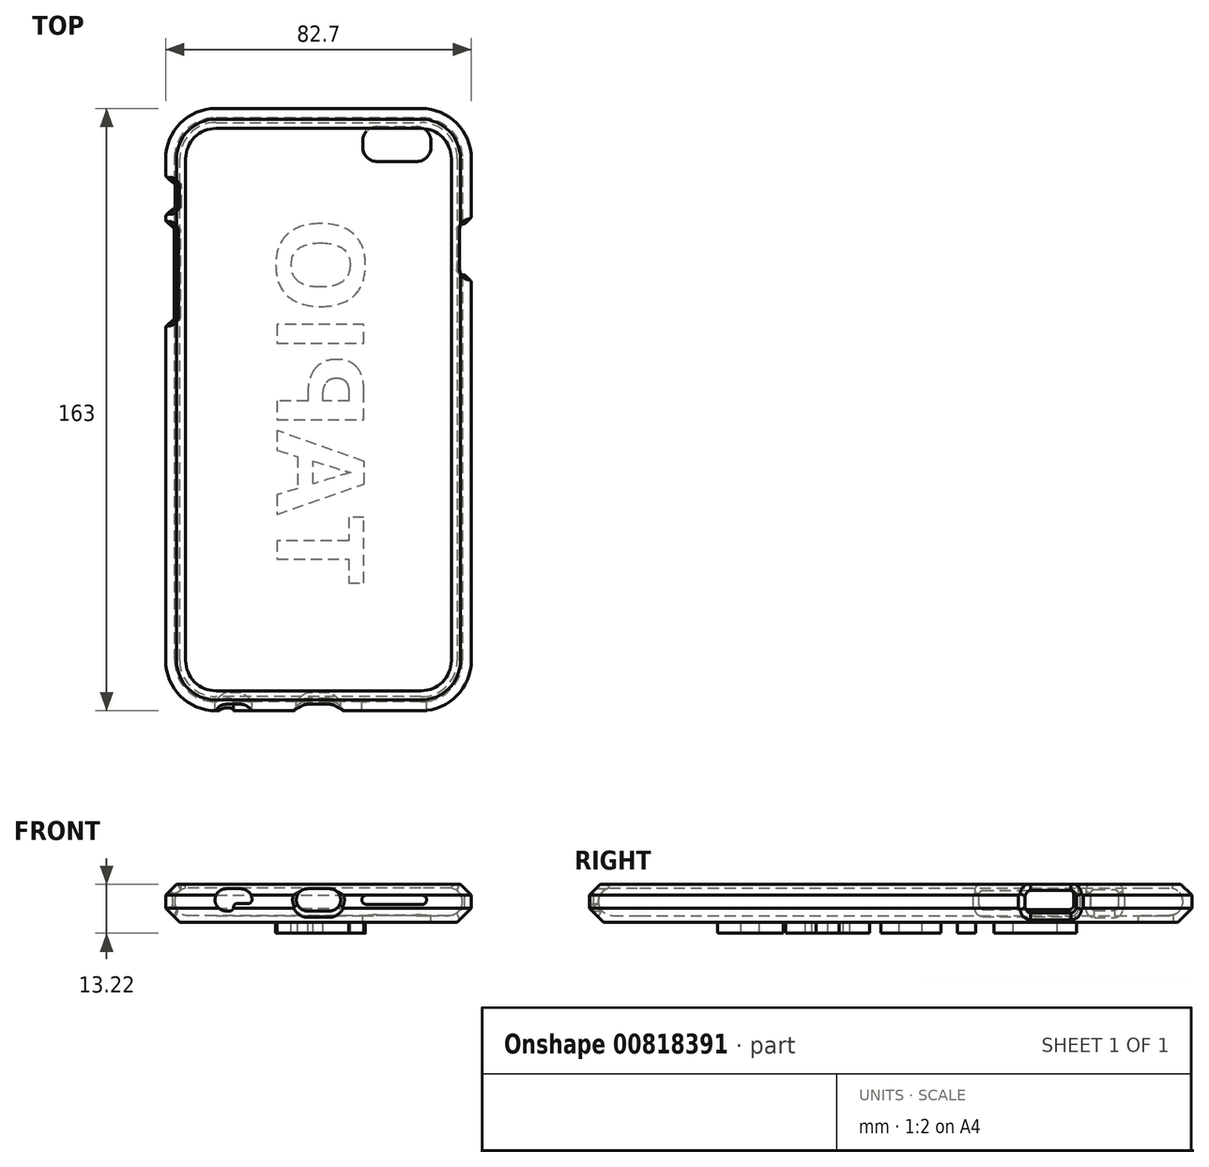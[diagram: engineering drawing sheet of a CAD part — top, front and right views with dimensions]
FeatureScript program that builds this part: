
annotation { "Feature Type Name" : "Feature", "Feature Type Description" : "" }
export const myFeature = defineFeature(function(context is Context, id is Id, definition is map)
    precondition{}
    {
        {
            assignVariable(context, id + "F0", {"name" : "HoleChamferLength", "anyValue" : 1.25});
        }
        {
            assignVariable(context, id + "F1", {"name" : "HoleChamferTopBottom", "anyValue" : 1.75});
        }
        {
            var Q0;
            Q0=qCreatedBy(makeId("Top.planeOp"),FACE);
            var sketch = newSketch(context, id + "F2", { "sketchPlane" : qUnion([Q0])});
            skLineSegment(sketch, "E0.bottom", {"start": v(27.75, 79.1) * mm, "end": v(0, 79.1) * mm});
            skLineSegment(sketch, "E0.top", {"start": v(27.75, -79.1) * mm, "end": v(-27.75, -79.1) * mm});
            skLineSegment(sketch, "E0.left", {"start": v(38.95, 67.9) * mm, "end": v(38.95, -67.9) * mm});
            skLineSegment(sketch, "E0.right", {"start": v(-38.95, 67.9) * mm, "end": v(-38.95, -67.9) * mm});
            skPoint(sketch, "E0.middle", {"position": v(0, 0) * mm});
            skPoint(sketch, "E1.visualSharp", {"position": v(-38.95, 79.1) * mm});
            skArc(sketch, "E1.filletArc", {"start": v(-27.75, 79.1) * mm, "mid": v(-35.67, 75.82) * mm, "end": v(-38.95, 67.9) * mm});
            skPoint(sketch, "E2.visualSharp", {"position": v(38.95, 79.1) * mm});
            skArc(sketch, "E2.filletArc", {"start": v(38.95, 67.9) * mm, "mid": v(35.67, 75.82) * mm, "end": v(27.75, 79.1) * mm});
            skPoint(sketch, "E3.visualSharp", {"position": v(38.95, -79.1) * mm});
            skArc(sketch, "E3.filletArc", {"start": v(27.75, -79.1) * mm, "mid": v(35.67, -75.82) * mm, "end": v(38.95, -67.9) * mm});
            skPoint(sketch, "E4.visualSharp", {"position": v(-38.95, -79.1) * mm});
            skArc(sketch, "E4.filletArc", {"start": v(-38.95, -67.9) * mm, "mid": v(-35.67, -75.82) * mm, "end": v(-27.75, -79.1) * mm});
            skLineSegment(sketch, "E5", {"start": v(0, 79.1) * mm, "end": v(-27.75, 79.1) * mm});
            skSolve(sketch);
        }
        {
            var Q0;
            Q0=qCreatedBy(makeId("Right.planeOp"),FACE);
            var sketch = newSketch(context, id + "F3", { "sketchPlane" : qUnion([Q0])});
            skPoint(sketch, "E6.0", {"position": v(79.1, 0) * mm});
            skArc(sketch, "E7", {"start": v(75.35, -3.75) * mm, "mid": v(79.1, 0) * mm, "end": v(75.35, 3.75) * mm});
            skLineSegment(sketch, "E8", {"start": v(75.35, -3.75) * mm, "end": v(75.35, 3.75) * mm, "construction": true});
            skLineSegment(sketch, "E9", {"start": v(81.5, -1.75) * mm, "end": v(81.5, 1.75) * mm});
            skLineSegment(sketch, "E10", {"start": v(81.5, 1.75) * mm, "end": v(79.75, 3.5) * mm});
            skLineSegment(sketch, "E11.trimOffspring", {"start": v(79.75, -3.5) * mm, "end": v(81.5, -1.75) * mm});
            skLineSegment(sketch, "E12", {"start": v(75.35, -5.55) * mm, "end": v(75.35, -3.75) * mm});
            skLineSegment(sketch, "E13", {"start": v(75.35, -5.55) * mm, "end": v(84.8, -5.55) * mm, "construction": true});
            skPoint(sketch, "E14", {"position": v(81.5, 0) * mm});
            skPoint(sketch, "E15.visualSharp", {"position": v(66.64, 4.7) * mm});
            skArc(sketch, "E15.filletArc", {"start": v(77.32, 4.67) * mm, "mid": v(76.53, 4.4) * mm, "end": v(76.1, 3.67) * mm});
            skLineSegment(sketch, "E16", {"start": v(79.75, -3.5) * mm, "end": v(77.7, -5.55) * mm});
            skLineSegment(sketch, "E17", {"start": v(77.7, -5.55) * mm, "end": v(75.35, -5.55) * mm});
            skLineSegment(sketch, "E18", {"start": v(79.75, 3.5) * mm, "end": v(78.58, 4.67) * mm});
            skLineSegment(sketch, "E19", {"start": v(78.58, 4.67) * mm, "end": v(77.32, 4.67) * mm});
            skLineSegment(sketch, "E20", {"start": v(76.1, 3.67) * mm, "end": v(66.64, 5.6) * mm, "construction": true});
            skSolve(sketch);
        }
        {
            var Q0;
            Q0=sQuery(id+"F2.wireOp",EDGE,"E5");
            var Q1;
            Q1=sQuery(id+"F2.wireOp",VERTEX,"E5.end");
            cPlane(context, id + "F4", {"entities" : qUnion([Q0, Q1]), "cplaneType" : CPlaneType.LINE_POINT, "offset" : 25 * mm, "width" : 150 * mm, "height" : 150 * mm});
        }
        {
            var Q0;
            Q0=sQuery(id+"F2.wireOp",EDGE,"E0.bottom");
            var Q1;
            Q1=sQuery(id+"F2.wireOp",VERTEX,"E2.filletArc.end");
            cPlane(context, id + "F5", {"entities" : qUnion([Q0, Q1]), "cplaneType" : CPlaneType.LINE_POINT, "offset" : 25 * mm, "width" : 150 * mm, "height" : 150 * mm});
        }
        {
            var Q0;
            Q0=sQuery(id+"F2.wireOp",EDGE,"E0.right");
            var Q1;
            Q1=sQuery(id+"F2.wireOp",VERTEX,"E0.right.end");
            cPlane(context, id + "F6", {"entities" : qUnion([Q0, Q1]), "cplaneType" : CPlaneType.LINE_POINT, "offset" : 25 * mm, "width" : 150 * mm, "height" : 150 * mm});
        }
        {
            var Q0;
            Q0=qCreatedBy(id+"F4.planeOp",FACE);
            var sketch = newSketch(context, id + "F7", { "sketchPlane" : qUnion([Q0])});
            skLineSegment(sketch, "E21.bottom", {"start": v(-24.95, -1.88) * mm, "end": v(-48.6, -1.88) * mm});
            skLineSegment(sketch, "E21.top", {"start": v(-24.95, 2.87) * mm, "end": v(-48.6, 2.87) * mm});
            skLineSegment(sketch, "E21.left", {"start": v(-23.95, -0.88) * mm, "end": v(-23.95, 1.87) * mm});
            skLineSegment(sketch, "E21.right", {"start": v(-49.6, -0.88) * mm, "end": v(-49.6, 1.87) * mm});
            skPoint(sketch, "E21.middle", {"position": v(-36.77, 0.5) * mm});
            skPoint(sketch, "E22.visualSharp", {"position": v(-49.6, 2.87) * mm});
            skArc(sketch, "E22.filletArc", {"start": v(-48.6, 2.87) * mm, "mid": v(-49.3, 2.58) * mm, "end": v(-49.6, 1.87) * mm});
            skPoint(sketch, "E23.visualSharp", {"position": v(-49.6, -1.88) * mm});
            skArc(sketch, "E23.filletArc", {"start": v(-49.6, -0.88) * mm, "mid": v(-49.3, -1.58) * mm, "end": v(-48.6, -1.88) * mm});
            skPoint(sketch, "E24.visualSharp", {"position": v(-23.95, 2.87) * mm});
            skArc(sketch, "E24.filletArc", {"start": v(-23.95, 1.87) * mm, "mid": v(-24.24, 2.58) * mm, "end": v(-24.95, 2.87) * mm});
            skPoint(sketch, "E25.visualSharp", {"position": v(-23.95, -1.88) * mm});
            skArc(sketch, "E25.filletArc", {"start": v(-24.95, -1.88) * mm, "mid": v(-24.24, -1.58) * mm, "end": v(-23.95, -0.88) * mm});
            skLineSegment(sketch, "E26.bottom", {"start": v(-60.6, 3.12) * mm, "end": v(-55.1, 3.12) * mm});
            skLineSegment(sketch, "E26.top", {"start": v(-60.6, -2.13) * mm, "end": v(-55.1, -2.13) * mm});
            skLineSegment(sketch, "E26.left", {"start": v(-61.6, 2.12) * mm, "end": v(-61.6, -1.13) * mm});
            skLineSegment(sketch, "E26.right", {"start": v(-54.1, 2.12) * mm, "end": v(-54.1, -1.13) * mm});
            skPoint(sketch, "E26.middle", {"position": v(-57.85, 0.5) * mm});
            skPoint(sketch, "E27.visualSharp", {"position": v(-61.6, 3.12) * mm});
            skArc(sketch, "E27.filletArc", {"start": v(-60.6, 3.13) * mm, "mid": v(-61.3, 2.83) * mm, "end": v(-61.6, 2.12) * mm});
            skPoint(sketch, "E28.visualSharp", {"position": v(-61.6, -2.13) * mm});
            skArc(sketch, "E28.filletArc", {"start": v(-61.6, -1.13) * mm, "mid": v(-61.3, -1.83) * mm, "end": v(-60.6, -2.13) * mm});
            skPoint(sketch, "E29.visualSharp", {"position": v(-54.1, -2.13) * mm});
            skArc(sketch, "E29.filletArc", {"start": v(-55.1, -2.13) * mm, "mid": v(-54.4, -1.83) * mm, "end": v(-54.1, -1.13) * mm});
            skPoint(sketch, "E30.visualSharp", {"position": v(-54.1, 3.12) * mm});
            skArc(sketch, "E30.filletArc", {"start": v(-54.1, 2.12) * mm, "mid": v(-54.4, 2.83) * mm, "end": v(-55.1, 3.13) * mm});
            skSolve(sketch);
        }
        {
            var Q0;
            Q0=qCreatedBy(id+"F5.planeOp",FACE);
            var sketch = newSketch(context, id + "F8", { "sketchPlane" : qUnion([Q0])});
            skLineSegment(sketch, "E31.bottom", {"start": v(-48.85, 2.75) * mm, "end": v(-37.85, 2.75) * mm});
            skLineSegment(sketch, "E31.top", {"start": v(-48.85, -2.75) * mm, "end": v(-37.85, -2.75) * mm});
            skLineSegment(sketch, "E31.left", {"start": v(-50.35, 1.25) * mm, "end": v(-50.35, -1.25) * mm});
            skLineSegment(sketch, "E31.right", {"start": v(-36.35, 1.25) * mm, "end": v(-36.35, -1.25) * mm});
            skPoint(sketch, "E31.middle", {"position": v(-43.35, 0) * mm});
            skPoint(sketch, "E32.visualSharp", {"position": v(-50.35, 2.75) * mm});
            skArc(sketch, "E32.filletArc", {"start": v(-48.85, 2.75) * mm, "mid": v(-49.91, 2.31) * mm, "end": v(-50.35, 1.25) * mm});
            skPoint(sketch, "E33.visualSharp", {"position": v(-50.35, -2.75) * mm});
            skArc(sketch, "E33.filletArc", {"start": v(-50.35, -1.25) * mm, "mid": v(-49.91, -2.31) * mm, "end": v(-48.85, -2.75) * mm});
            skPoint(sketch, "E34.visualSharp", {"position": v(-36.35, -2.75) * mm});
            skArc(sketch, "E34.filletArc", {"start": v(-37.85, -2.75) * mm, "mid": v(-36.79, -2.31) * mm, "end": v(-36.35, -1.25) * mm});
            skPoint(sketch, "E35.visualSharp", {"position": v(-36.35, 2.75) * mm});
            skArc(sketch, "E35.filletArc", {"start": v(-36.35, 1.25) * mm, "mid": v(-36.79, 2.31) * mm, "end": v(-37.85, 2.75) * mm});
            skSolve(sketch);
        }
        {
            var Q0;
            Q0=qCreatedBy(id+"F6.planeOp",FACE);
            var sketch = newSketch(context, id + "F9", { "sketchPlane" : qUnion([Q0])});
            skLineSegment(sketch, "E36.bottom", {"start": v(3, 3.5) * mm, "end": v(-3, 3.5) * mm});
            skLineSegment(sketch, "E36.top", {"start": v(3, -2.5) * mm, "end": v(-3, -2.5) * mm});
            skLineSegment(sketch, "E36.left", {"start": v(6, 0.5) * mm, "end": v(6, 0.5) * mm});
            skLineSegment(sketch, "E36.right", {"start": v(-6, 0.5) * mm, "end": v(-6, 0.5) * mm});
            skPoint(sketch, "E36.middle", {"position": v(0, 0.5) * mm});
            skArc(sketch, "E37", {"start": v(-25, 3.5) * mm, "mid": v(-28, 0.5) * mm, "end": v(-25, -2.5) * mm});
            skPoint(sketch, "E38.visualSharp", {"position": v(-6, 3.5) * mm});
            skArc(sketch, "E38.filletArc", {"start": v(-3, 3.5) * mm, "mid": v(-5.12, 2.62) * mm, "end": v(-6, 0.5) * mm});
            skPoint(sketch, "E39.visualSharp", {"position": v(-6, -2.5) * mm});
            skArc(sketch, "E39.filletArc", {"start": v(-6, 0.5) * mm, "mid": v(-5.12, -1.62) * mm, "end": v(-3, -2.5) * mm});
            skPoint(sketch, "E40.visualSharp", {"position": v(6, -2.5) * mm});
            skArc(sketch, "E40.filletArc", {"start": v(3, -2.5) * mm, "mid": v(5.12, -1.62) * mm, "end": v(6, 0.5) * mm});
            skPoint(sketch, "E41.visualSharp", {"position": v(6, 3.5) * mm});
            skArc(sketch, "E41.filletArc", {"start": v(6, 0.5) * mm, "mid": v(5.12, 2.62) * mm, "end": v(3, 3.5) * mm});
            skArc(sketch, "E42", {"start": v(-21, -2.5) * mm, "mid": v(-19.27, -1.95) * mm, "end": v(-18.17, -0.5) * mm, "construction": true});
            skLineSegment(sketch, "E43", {"start": v(-21, 3.5) * mm, "end": v(-25, 3.5) * mm});
            skLineSegment(sketch, "E44", {"start": v(-21, -2.5) * mm, "end": v(-23, -2.5) * mm, "construction": true});
            skLineSegment(sketch, "E45", {"start": v(13, 0.5) * mm, "end": v(28, 0.5) * mm, "construction": true});
            skArc(sketch, "E46.0.startCap", {"start": v(13, -0.75) * mm, "mid": v(11.75, 0.5) * mm, "end": v(13, 1.75) * mm});
            skArc(sketch, "E46.0.endCap", {"start": v(28, 1.75) * mm, "mid": v(29.25, 0.5) * mm, "end": v(28, -0.75) * mm});
            skLineSegment(sketch, "E46.0.left", {"start": v(13, 1.75) * mm, "end": v(28, 1.75) * mm});
            skLineSegment(sketch, "E46.0.right", {"start": v(13, -0.75) * mm, "end": v(28, -0.75) * mm});
            skLineSegment(sketch, "E47", {"start": v(-23, -1.5) * mm, "end": v(-23, -1.5) * mm});
            skLineSegment(sketch, "E48", {"start": v(-22, -0.5) * mm, "end": v(-19, -0.5) * mm});
            skLineSegment(sketch, "E49", {"start": v(-24, -2.5) * mm, "end": v(-25, -2.5) * mm});
            skArc(sketch, "E50", {"start": v(-18, 0.5) * mm, "mid": v(-18.88, 2.62) * mm, "end": v(-21, 3.5) * mm});
            skPoint(sketch, "E51.visualSharp", {"position": v(-23, -0.5) * mm});
            skArc(sketch, "E51.filletArc", {"start": v(-22, -0.5) * mm, "mid": v(-22.7, -0.8) * mm, "end": v(-23, -1.5) * mm});
            skPoint(sketch, "E52.visualSharp", {"position": v(-23, -2.5) * mm});
            skArc(sketch, "E52.filletArc", {"start": v(-24, -2.5) * mm, "mid": v(-23.3, -2.2) * mm, "end": v(-23, -1.5) * mm});
            skPoint(sketch, "E53.visualSharp", {"position": v(-18.17, -0.5) * mm});
            skArc(sketch, "E53.filletArc", {"start": v(-19, -0.5) * mm, "mid": v(-18.3, -0.2) * mm, "end": v(-18, 0.5) * mm});
            skCircle(sketch, "E54", {"center": v(-25, 0.5) * mm, "radius": 2.5 * mm, "construction": true});
            skSolve(sketch);
        }
        {
            var Q0;
            Q0=qCreatedBy(makeId("Top.planeOp"),FACE);
            var sketch = newSketch(context, id + "F10", { "sketchPlane" : qUnion([Q0])});
            skLineSegment(sketch, "E55.bottom", {"start": v(26.45, 67.1) * mm, "end": v(15.95, 67.1) * mm});
            skLineSegment(sketch, "E55.top", {"start": v(26.45, 76.6) * mm, "end": v(15.95, 76.6) * mm});
            skLineSegment(sketch, "E55.left", {"start": v(30.45, 71.1) * mm, "end": v(30.45, 72.6) * mm});
            skLineSegment(sketch, "E55.right", {"start": v(11.95, 71.1) * mm, "end": v(11.95, 72.6) * mm});
            skPoint(sketch, "E55.middle", {"position": v(21.2, 71.85) * mm});
            skPoint(sketch, "E56.visualSharp", {"position": v(11.95, 76.6) * mm});
            skArc(sketch, "E56.filletArc", {"start": v(15.95, 76.6) * mm, "mid": v(13.12, 75.43) * mm, "end": v(11.95, 72.6) * mm});
            skPoint(sketch, "E57.visualSharp", {"position": v(11.95, 67.1) * mm});
            skArc(sketch, "E57.filletArc", {"start": v(11.95, 71.1) * mm, "mid": v(13.12, 68.27) * mm, "end": v(15.95, 67.1) * mm});
            skPoint(sketch, "E58.visualSharp", {"position": v(30.45, 67.1) * mm});
            skArc(sketch, "E58.filletArc", {"start": v(26.45, 67.1) * mm, "mid": v(29.28, 68.27) * mm, "end": v(30.45, 71.1) * mm});
            skPoint(sketch, "E59.visualSharp", {"position": v(30.45, 76.6) * mm});
            skArc(sketch, "E59.filletArc", {"start": v(30.45, 72.6) * mm, "mid": v(29.28, 75.43) * mm, "end": v(26.45, 76.6) * mm});
            skSolve(sketch);
        }
        {
            var Q0;
            Q0=qSketchRegion(id+"F3",true);
            var Q1;
            Q1=sQuery(id+"F2.wireOp",EDGE,"E5");
            var Q2;
            Q2=sQuery(id+"F2.wireOp",EDGE,"E1.filletArc");
            var Q3;
            Q3=sQuery(id+"F2.wireOp",EDGE,"E0.right");
            var Q4;
            Q4=sQuery(id+"F2.wireOp",EDGE,"E4.filletArc");
            var Q5;
            Q5=sQuery(id+"F2.wireOp",EDGE,"E0.top");
            var Q6;
            Q6=sQuery(id+"F2.wireOp",EDGE,"E3.filletArc");
            var Q7;
            Q7=sQuery(id+"F2.wireOp",EDGE,"E0.left");
            var Q8;
            Q8=sQuery(id+"F2.wireOp",EDGE,"E2.filletArc");
            var Q9;
            Q9=sQuery(id+"F2.wireOp",EDGE,"E0.bottom");
            sweep(context, id + "F11", {"profiles" : qUnion([Q0]), "path" : qUnion([Q1, Q2, Q3, Q4, Q5, Q6, Q7, Q8, Q9])});
        }
        {
            var Q0;
            Q0=qCreatedBy(makeId("Front.planeOp"),FACE);
            var sketch = newSketch(context, id + "F12", { "sketchPlane" : qUnion([Q0])});
            skLineSegment(sketch, "E60.0.0", {"start": v(35.2, -5.55) * mm, "end": v(27.75, -5.55) * mm});
            skLineSegment(sketch, "E60.0.1", {"start": v(27.75, -3.75) * mm, "end": v(27.75, -5.55) * mm});
            skLineSegment(sketch, "E60.0.2", {"start": v(27.75, -3.75) * mm, "end": v(35.2, -3.75) * mm});
            skLineSegment(sketch, "E60.0.3", {"start": v(35.2, -3.75) * mm, "end": v(35.2, -5.55) * mm});
            skLineSegment(sketch, "E60.1.0", {"start": v(27.75, -5.55) * mm, "end": v(-27.75, -5.55) * mm});
            skLineSegment(sketch, "E60.1.1", {"start": v(-27.75, -3.75) * mm, "end": v(-27.75, -5.55) * mm});
            skLineSegment(sketch, "E60.1.2", {"start": v(-27.75, -3.75) * mm, "end": v(27.75, -3.75) * mm});
            skLineSegment(sketch, "E60.1.3", {"start": v(27.75, -3.75) * mm, "end": v(27.75, -5.55) * mm});
            skLineSegment(sketch, "E60.2.0", {"start": v(-27.75, -5.55) * mm, "end": v(-35.2, -5.55) * mm});
            skLineSegment(sketch, "E60.2.1", {"start": v(-35.2, -3.75) * mm, "end": v(-35.2, -5.55) * mm});
            skLineSegment(sketch, "E60.2.2", {"start": v(-35.2, -3.75) * mm, "end": v(-27.75, -3.75) * mm});
            skLineSegment(sketch, "E60.2.3", {"start": v(-27.75, -3.75) * mm, "end": v(-27.75, -5.55) * mm});
            skSolve(sketch);
        }
        {
            var Q0;
            Q0=qSketchRegion(id+"F12",true);
            extrude(context, id + "F13", {"entities" : qUnion([Q0]), "operationType" : NewBodyOperationType.ADD, "endBound" : BoundingType.UP_TO_NEXT, "depth" : 25 * mm, "hasSecondDirection" : true, "secondDirectionBound" : SecondDirectionBoundingType.UP_TO_NEXT, "secondDirectionOppositeDirection" : true, "secondDirectionDepth" : 25 * mm});
        }
        {
            var Q0;
            Q0=qSketchRegion(id+"F7",true);
            extrude(context, id + "F14", {"entities" : qUnion([Q0]), "operationType" : NewBodyOperationType.REMOVE, "endBound" : BoundingType.THROUGH_ALL, "depth" : 25 * mm});
        }
        {
            var Q0;
            Q0=qSketchRegion(id+"F8",true);
            extrude(context, id + "F15", {"entities" : qUnion([Q0]), "operationType" : NewBodyOperationType.REMOVE, "endBound" : BoundingType.THROUGH_ALL, "oppositeDirection" : true, "depth" : 25 * mm});
        }
        {
            var Q0;
            Q0=makeQuery(id+"F10.imprint","IMPRINT",FACE,{"disambiguationData":[TD([[makeQuery(id+"F10.imprint","IMPRINT",EDGE,{"derivedFrom":sQuery(id+"F10.wireOp",EDGE,"E55.bottom")}),-1.0]])]});
            extrude(context, id + "F16", {"entities" : qUnion([Q0]), "operationType" : NewBodyOperationType.REMOVE, "endBound" : BoundingType.THROUGH_ALL, "oppositeDirection" : true, "depth" : 25 * mm});
        }
        {
            var Q0;
            Q0=qSketchRegion(id+"F9",true);
            extrude(context, id + "F17", {"entities" : qUnion([Q0]), "operationType" : NewBodyOperationType.REMOVE, "endBound" : BoundingType.THROUGH_ALL, "depth" : 25 * mm});
        }
        {
            var Q0;
            Q0=makeQuery(id+"F14.boolean.opBoolean","INTERSECT",EDGE,{"derivedFrom":[makeQuery(id+"F11.opSweep","SWEPT_FACE",FACE,{"disambiguationData":[OSD([sQuery(id+"F2.wireOp",EDGE,"E0.right"),sQuery(id+"F3.wireOp",EDGE,"E11.trimOffspring"),sQuery(id+"F3.wireOp",EDGE,"E16")])]}),makeQuery(id+"F14.opExtrude","SWEPT_FACE",FACE,{"disambiguationData":[OSD([sQuery(id+"F7.wireOp",EDGE,"E21.bottom")])]})]});
            var Q1;
            Q1=makeQuery(id+"F14.boolean.opBoolean","INTERSECT",EDGE,{"derivedFrom":[makeQuery(id+"F11.opSweep","SWEPT_FACE",FACE,{"disambiguationData":[OSD([sQuery(id+"F2.wireOp",EDGE,"E0.right"),sQuery(id+"F3.wireOp",EDGE,"E10")])]}),makeQuery(id+"F14.opExtrude","SWEPT_FACE",FACE,{"disambiguationData":[OSD([sQuery(id+"F7.wireOp",EDGE,"E21.top")])]})]});
            chamfer(context, id + "F18", {"entities" : qUnion([Q0, Q1]), "width" : (getVariable(context, 'HoleChamferLength')) * mm, "tangentPropagation" : true});
        }
        {
            var Q0;
            Q0=makeQuery(id+"F14.boolean.opBoolean","INTERSECT",EDGE,{"derivedFrom":[makeQuery(id+"F11.opSweep","SWEPT_FACE",FACE,{"disambiguationData":[OSD([sQuery(id+"F2.wireOp",EDGE,"E0.right"),sQuery(id+"F3.wireOp",EDGE,"E11.trimOffspring"),sQuery(id+"F3.wireOp",EDGE,"E16")])]}),makeQuery(id+"F14.opExtrude","SWEPT_FACE",FACE,{"disambiguationData":[OSD([sQuery(id+"F7.wireOp",EDGE,"E26.top")])]})]});
            var Q1;
            Q1=makeQuery(id+"F14.boolean.opBoolean","INTERSECT",EDGE,{"derivedFrom":[makeQuery(id+"F11.opSweep","SWEPT_FACE",FACE,{"disambiguationData":[OSD([sQuery(id+"F2.wireOp",EDGE,"E0.right"),sQuery(id+"F3.wireOp",EDGE,"E10")])]}),makeQuery(id+"F14.opExtrude","SWEPT_FACE",FACE,{"disambiguationData":[OSD([sQuery(id+"F7.wireOp",EDGE,"E26.bottom")])]})]});
            chamfer(context, id + "F19", {"entities" : qUnion([Q0, Q1]), "width" : (getVariable(context, 'HoleChamferLength')) * mm, "tangentPropagation" : true});
        }
        {
            var Q0;
            Q0=makeQuery(id+"F15.boolean.opBoolean","INTERSECT",EDGE,{"derivedFrom":[makeQuery(id+"F11.opSweep","SWEPT_FACE",FACE,{"disambiguationData":[OSD([sQuery(id+"F2.wireOp",EDGE,"E0.left"),sQuery(id+"F3.wireOp",EDGE,"E11.trimOffspring"),sQuery(id+"F3.wireOp",EDGE,"E16")])]}),makeQuery(id+"F15.opExtrude","SWEPT_FACE",FACE,{"disambiguationData":[OSD([sQuery(id+"F8.wireOp",EDGE,"E31.top")])]})]});
            var Q1;
            Q1=makeQuery(id+"F15.boolean.opBoolean","INTERSECT",EDGE,{"derivedFrom":[makeQuery(id+"F11.opSweep","SWEPT_FACE",FACE,{"disambiguationData":[OSD([sQuery(id+"F2.wireOp",EDGE,"E0.left"),sQuery(id+"F3.wireOp",EDGE,"E10")])]}),makeQuery(id+"F15.opExtrude","SWEPT_FACE",FACE,{"disambiguationData":[OSD([sQuery(id+"F8.wireOp",EDGE,"E31.bottom")])]})]});
            chamfer(context, id + "F20", {"entities" : qUnion([Q0, Q1]), "width" : (getVariable(context, 'HoleChamferLength')) * mm, "tangentPropagation" : true});
        }
        {
            var Q0;
            Q0=makeQuery(id+"F15.boolean.opBoolean","INTERSECT",EDGE,{"derivedFrom":[makeQuery(id+"F11.opSweep","SWEPT_FACE",FACE,{"disambiguationData":[OSD([sQuery(id+"F2.wireOp",EDGE,"E0.left"),sQuery(id+"F3.wireOp",EDGE,"E9")])]}),makeQuery(id+"F15.opExtrude","SWEPT_FACE",FACE,{"disambiguationData":[OSD([sQuery(id+"F8.wireOp",EDGE,"E31.left")])]})]});
            var Q1;
            Q1=makeQuery(id+"F15.boolean.opBoolean","INTERSECT",EDGE,{"derivedFrom":[makeQuery(id+"F11.opSweep","SWEPT_FACE",FACE,{"disambiguationData":[OSD([sQuery(id+"F2.wireOp",EDGE,"E0.left"),sQuery(id+"F3.wireOp",EDGE,"E9")])]}),makeQuery(id+"F15.opExtrude","SWEPT_FACE",FACE,{"disambiguationData":[OSD([sQuery(id+"F8.wireOp",EDGE,"E31.right")])]})]});
            var Q2;
            Q2=makeQuery(id+"F14.boolean.opBoolean","INTERSECT",EDGE,{"derivedFrom":[makeQuery(id+"F11.opSweep","SWEPT_FACE",FACE,{"disambiguationData":[OSD([sQuery(id+"F2.wireOp",EDGE,"E0.right"),sQuery(id+"F3.wireOp",EDGE,"E9")])]}),makeQuery(id+"F14.opExtrude","SWEPT_FACE",FACE,{"disambiguationData":[OSD([sQuery(id+"F7.wireOp",EDGE,"E21.left")])]})]});
            var Q3;
            Q3=makeQuery(id+"F14.boolean.opBoolean","INTERSECT",EDGE,{"derivedFrom":[makeQuery(id+"F11.opSweep","SWEPT_FACE",FACE,{"disambiguationData":[OSD([sQuery(id+"F2.wireOp",EDGE,"E0.right"),sQuery(id+"F3.wireOp",EDGE,"E9")])]}),makeQuery(id+"F14.opExtrude","SWEPT_FACE",FACE,{"disambiguationData":[OSD([sQuery(id+"F7.wireOp",EDGE,"E21.right")])]})]});
            var Q4;
            Q4=makeQuery(id+"F14.boolean.opBoolean","INTERSECT",EDGE,{"derivedFrom":[makeQuery(id+"F11.opSweep","SWEPT_FACE",FACE,{"disambiguationData":[OSD([sQuery(id+"F2.wireOp",EDGE,"E0.right"),sQuery(id+"F3.wireOp",EDGE,"E9")])]}),makeQuery(id+"F14.opExtrude","SWEPT_FACE",FACE,{"disambiguationData":[OSD([sQuery(id+"F7.wireOp",EDGE,"E26.left")])]})]});
            var Q5;
            Q5=makeQuery(id+"F14.boolean.opBoolean","INTERSECT",EDGE,{"derivedFrom":[makeQuery(id+"F11.opSweep","SWEPT_FACE",FACE,{"disambiguationData":[OSD([sQuery(id+"F2.wireOp",EDGE,"E0.right"),sQuery(id+"F3.wireOp",EDGE,"E9")])]}),makeQuery(id+"F14.opExtrude","SWEPT_FACE",FACE,{"disambiguationData":[OSD([sQuery(id+"F7.wireOp",EDGE,"E26.right")])]})]});
            chamfer(context, id + "F21", {"entities" : qUnion([Q0, Q1, Q2, Q3, Q4, Q5]), "width" : (getVariable(context, 'HoleChamferTopBottom')) * mm, "tangentPropagation" : true});
        }
        {
            var Q0;
            Q0=makeQuery(id+"F17.boolean.opBoolean","INTERSECT",EDGE,{"derivedFrom":[makeQuery(id+"F11.opSweep","SWEPT_FACE",FACE,{"disambiguationData":[OSD([sQuery(id+"F2.wireOp",EDGE,"E0.top"),sQuery(id+"F3.wireOp",EDGE,"E11.trimOffspring"),sQuery(id+"F3.wireOp",EDGE,"E16")])]}),makeQuery(id+"F17.opExtrude","SWEPT_FACE",FACE,{"disambiguationData":[OSD([sQuery(id+"F9.wireOp",EDGE,"E36.top")])]})]});
            var Q1;
            Q1=makeQuery(id+"F17.boolean.opBoolean","INTERSECT",EDGE,{"derivedFrom":[makeQuery(id+"F11.opSweep","SWEPT_FACE",FACE,{"disambiguationData":[OSD([sQuery(id+"F2.wireOp",EDGE,"E0.top"),sQuery(id+"F3.wireOp",EDGE,"E9")])]}),makeQuery(id+"F17.opExtrude","SWEPT_FACE",FACE,{"disambiguationData":[OSD([sQuery(id+"F9.wireOp",EDGE,"E38.filletArc"),sQuery(id+"F9.wireOp",EDGE,"E39.filletArc")])]})]});
            var Q2;
            Q2=makeQuery(id+"F17.boolean.opBoolean","INTERSECT",EDGE,{"derivedFrom":[makeQuery(id+"F11.opSweep","SWEPT_FACE",FACE,{"disambiguationData":[OSD([sQuery(id+"F2.wireOp",EDGE,"E0.top"),sQuery(id+"F3.wireOp",EDGE,"E9")])]}),makeQuery(id+"F17.opExtrude","SWEPT_FACE",FACE,{"disambiguationData":[OSD([sQuery(id+"F9.wireOp",EDGE,"E40.filletArc"),sQuery(id+"F9.wireOp",EDGE,"E41.filletArc")])]})]});
            chamfer(context, id + "F22", {"entities" : qUnion([Q0, Q1, Q2]), "width" : 1 * mm, "tangentPropagation" : true});
        }
        {
            var Q0;
            Q0=qCreatedBy(makeId("Right.planeOp"),FACE);
            var sketch = newSketch(context, id + "F23", { "sketchPlane" : qUnion([Q0])});
            skLineSegment(sketch, "E61", {"start": v(73.83, -4.65) * mm, "end": v(73.23, -4.65) * mm});
            skLineSegment(sketch, "E62", {"start": v(72.71, -5.55) * mm, "end": v(74.35, -5.55) * mm});
            skLineSegment(sketch, "E63", {"start": v(74.35, -5.55) * mm, "end": v(73.83, -4.65) * mm});
            skLineSegment(sketch, "E64", {"start": v(73.23, -4.65) * mm, "end": v(72.71, -5.55) * mm});
            skSolve(sketch);
        }
        {
            var Q0;
            Q0=makeQuery(id+"F13.boolean.opBoolean","MERGE",FACE,{"derivedFrom":[makeQuery(id+"F11.opSweep","SWEPT_FACE",FACE,{"disambiguationData":[OSD([sQuery(id+"F2.wireOp",EDGE,"E0.bottom"),sQuery(id+"F3.wireOp",EDGE,"E17")])]}),makeQuery(id+"F13.opExtrude","SWEPT_FACE",FACE,{"disambiguationData":[OSD([sQuery(id+"F12.wireOp",EDGE,"E60.0.0"),sQuery(id+"F12.wireOp",EDGE,"E60.1.0"),sQuery(id+"F12.wireOp",EDGE,"E60.2.0")])]})]});
            var sketch = newSketch(context, id + "F24", { "sketchPlane" : qUnion([Q0])});
            skText(sketch, "E65", { "text": "TAPIO", "fontName": "OpenSans-Bold.ttf"});
            const initialGuessF24  = {"E65": [-0.01124, 0.04754, 0, -1, 0.02376]};
            skSetInitialGuess(sketch, initialGuessF24);
            skSolve(sketch);
        }
        {
            var Q0;
            Q0 = qSketchRegion(id + "F24", true);
            extrude(context, id + "F25", {"entities" : qUnion([Q0]), "operationType" : NewBodyOperationType.ADD, "depth" : 3 * mm, "offsetDistance" : 25 * mm});
        }
    });
